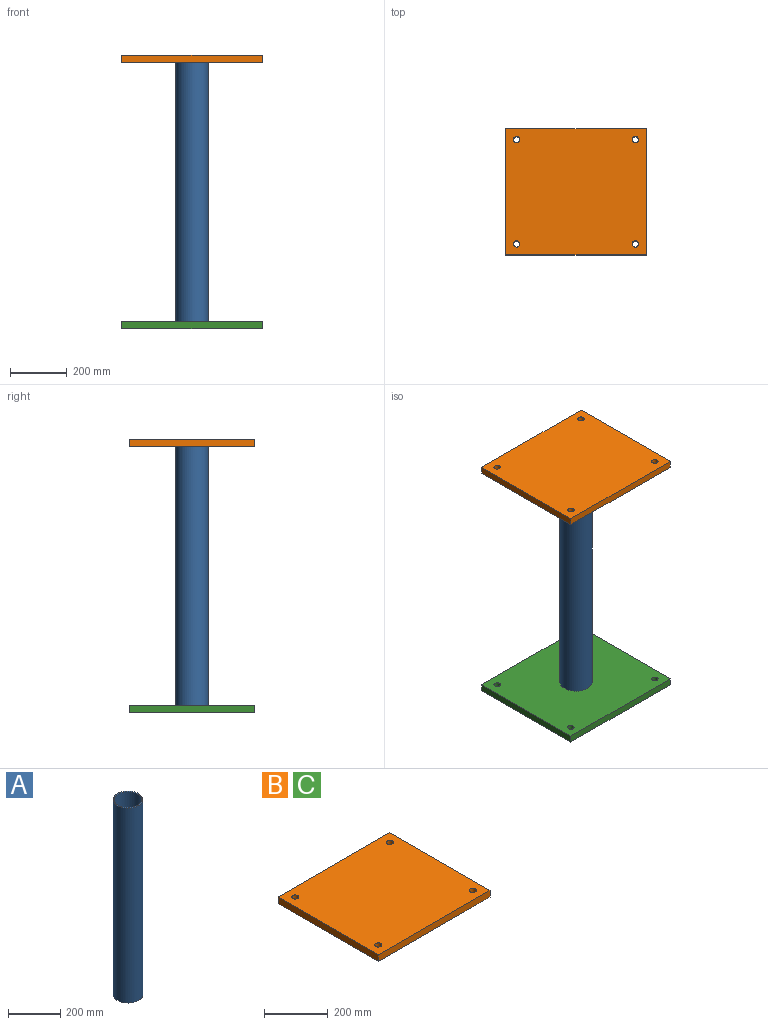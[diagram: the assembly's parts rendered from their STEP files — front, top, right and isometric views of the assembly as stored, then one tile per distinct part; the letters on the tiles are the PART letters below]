
ASSEMBLY  parts=3 mates=2
PART A: 4 faces, bbox 114.3x114.3x914.4 mm
  f0: cylinder r=57.15mm len=914.4mm, axis (0,0,-1), area 328346.4mm2, adj f1,f2
  f1: plane 114.3x114.3mm, normal (0,0,1), area 1638.9mm2, adj f0,f3
  f2: plane 114.3x114.3mm, normal (0,0,-1), area 1638.9mm2, adj f0,f3
  f3: cylinder r=52.39mm len=914.4mm, axis (0,0,1), area 300984.2mm2, adj f1,f2
PART B: 10 faces, bbox 495.3x444.5x25.4 mm
  f0: plane 495.3x25.4mm, normal (0,1,0), area 12580.6mm2, adj f1,f3,f4,f5
  f1: plane 444.5x25.4mm, normal (-1,0,0), area 11290.3mm2, adj f0,f2,f4,f5
  f2: plane 495.3x25.4mm, normal (0,-1,0), area 12580.6mm2, adj f1,f3,f4,f5
  f3: plane 444.5x25.4mm, normal (1,0,0), area 11290.3mm2, adj f0,f2,f4,f5
  f4: plane 495.3x444.5mm, normal (0,0,1), area 218598.4mm2, adj f0,f1,f2,f3,f6,f7,f8,f9
  f5: plane 495.3x444.5mm, normal (0,0,-1), area 218598.4mm2, adj f0,f1,f2,f3,f6,f7,f8,f9
  f6: cylinder r=11.15mm len=25.4mm, axis (0,0,1), area 1779.6mm2, adj f4,f5
  f7: cylinder r=11.15mm len=25.4mm, axis (0,0,1), area 1779.6mm2, adj f4,f5
  f8: cylinder r=11.15mm len=25.4mm, axis (0,0,1), area 1779.6mm2, adj f4,f5
  f9: cylinder r=11.15mm len=25.4mm, axis (0,0,1), area 1779.6mm2, adj f4,f5
PART C: same geometry as B
PLACE A t=(-5.46,9.46,18.92)mm fixed
PLACE B t=(-5.46,9.46,488.82)mm
PLACE C t=(-5.46,9.46,-450.98)mm
MATE fastened A.f0 <-> C.f4  axis (0,0,-1) through (-5.46,9.46,-438.28)mm
MATE fastened A.f0 <-> B.f5  axis (0,0,1) through (-5.46,9.46,476.12)mm
